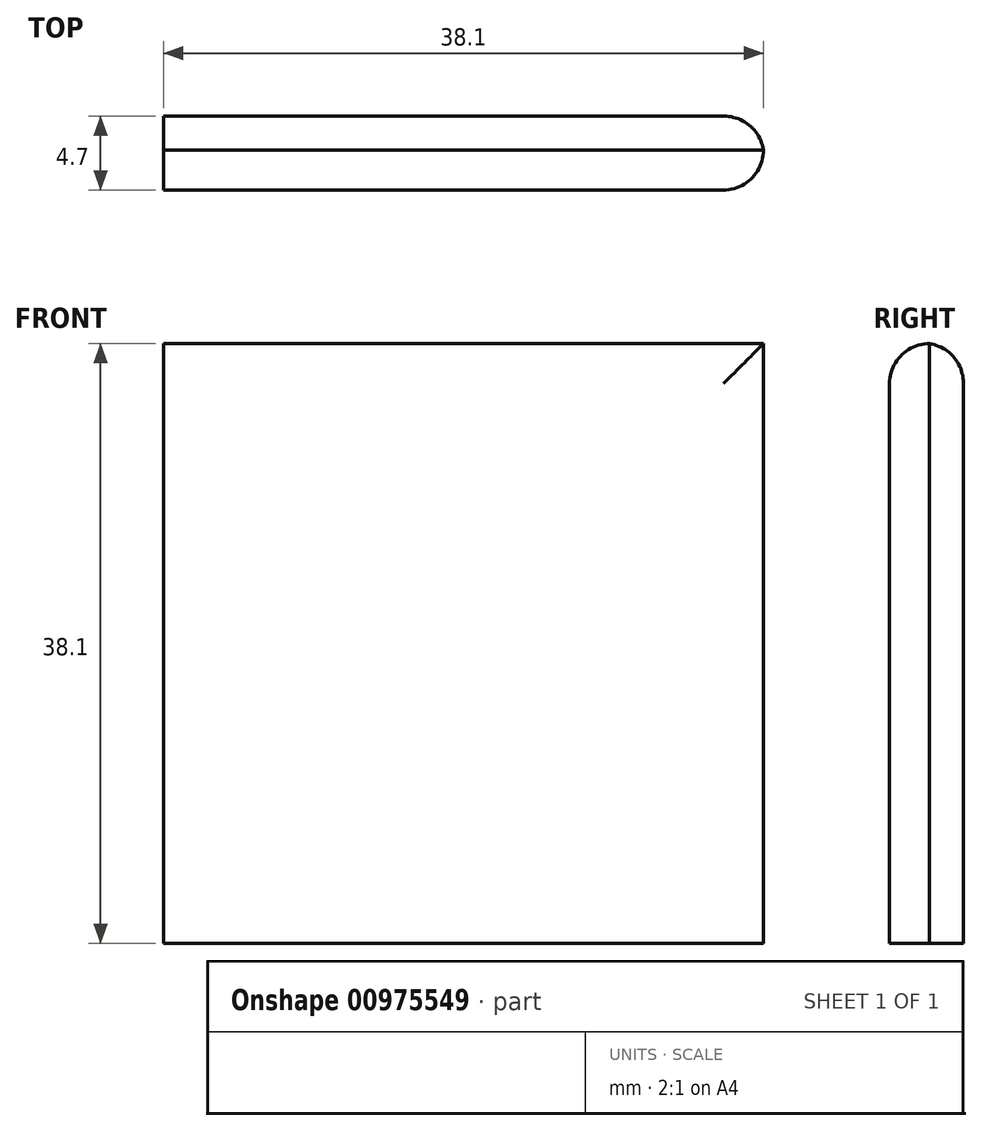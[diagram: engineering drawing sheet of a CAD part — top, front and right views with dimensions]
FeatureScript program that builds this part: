
annotation { "Feature Type Name" : "Feature", "Feature Type Description" : "" }
export const myFeature = defineFeature(function(context is Context, id is Id, definition is map)
    precondition{}
    {
        {
            var Q0;
            Q0=qCreatedBy(makeId("Front.planeOp"),FACE);
            var sketch = newSketch(context, id + "F0", { "sketchPlane" : qUnion([Q0])});
            skLineSegment(sketch, "E0.bottom", {"start": v(-19.05, 19.05) * mm, "end": v(19.05, 19.05) * mm});
            skLineSegment(sketch, "E0.top", {"start": v(-19.05, -19.05) * mm, "end": v(19.05, -19.05) * mm});
            skLineSegment(sketch, "E0.left", {"start": v(-19.05, 19.05) * mm, "end": v(-19.05, -19.05) * mm});
            skLineSegment(sketch, "E0.right", {"start": v(19.05, 19.05) * mm, "end": v(19.05, -19.05) * mm});
            skSolve(sketch);
        }
        {
            var Q0;
            Q0=makeQuery(id+"F0.imprint","IMPRINT",FACE,{"disambiguationData":[TD([[makeQuery(id+"F0.imprint","IMPRINT",EDGE,{"derivedFrom":sQuery(id+"F0.wireOp",EDGE,"E0.bottom")}),-1.0]])]});
            extrude(context, id + "F1", {"entities" : qUnion([Q0]), "depth" : 4.7 * mm, "offsetDistance" : 25.4 * mm});
        }
        {
            var Q0;
            Q0=makeQuery(id+"F1.opExtrude","CAP_EDGE",EDGE,{"disambiguationData":[OSD([sQuery(id+"F0.wireOp",EDGE,"E0.right")])],"isStart":false});
            fillet(context, id + "F2", {"entities" : qUnion([Q0]), "radius" : 2.54 * mm, "tangentPropagation" : true, "allowEdgeOverflow" : false});
        }
        {
            var Q0;
            Q0=makeQuery(id+"F1.opExtrude","CAP_EDGE",EDGE,{"disambiguationData":[OSD([sQuery(id+"F0.wireOp",EDGE,"E0.right")])],"isStart":true});
            fillet(context, id + "F3", {"entities" : qUnion([Q0]), "radius" : 2.54 * mm, "tangentPropagation" : true, "allowEdgeOverflow" : false});
        }
        {
            var Q0;
            Q0=makeQuery(id+"F1.opExtrude","CAP_EDGE",EDGE,{"disambiguationData":[OSD([sQuery(id+"F0.wireOp",EDGE,"E0.bottom")])],"isStart":false});
            fillet(context, id + "F4", {"entities" : qUnion([Q0]), "radius" : 2.54 * mm, "tangentPropagation" : true, "allowEdgeOverflow" : false});
        }
        {
            var Q0;
            Q0=makeQuery(id+"F1.opExtrude","CAP_EDGE",EDGE,{"disambiguationData":[OSD([sQuery(id+"F0.wireOp",EDGE,"E0.bottom")])],"isStart":true});
            fillet(context, id + "F5", {"entities" : qUnion([Q0]), "radius" : 2.54 * mm, "tangentPropagation" : true, "allowEdgeOverflow" : false});
        }
    });
